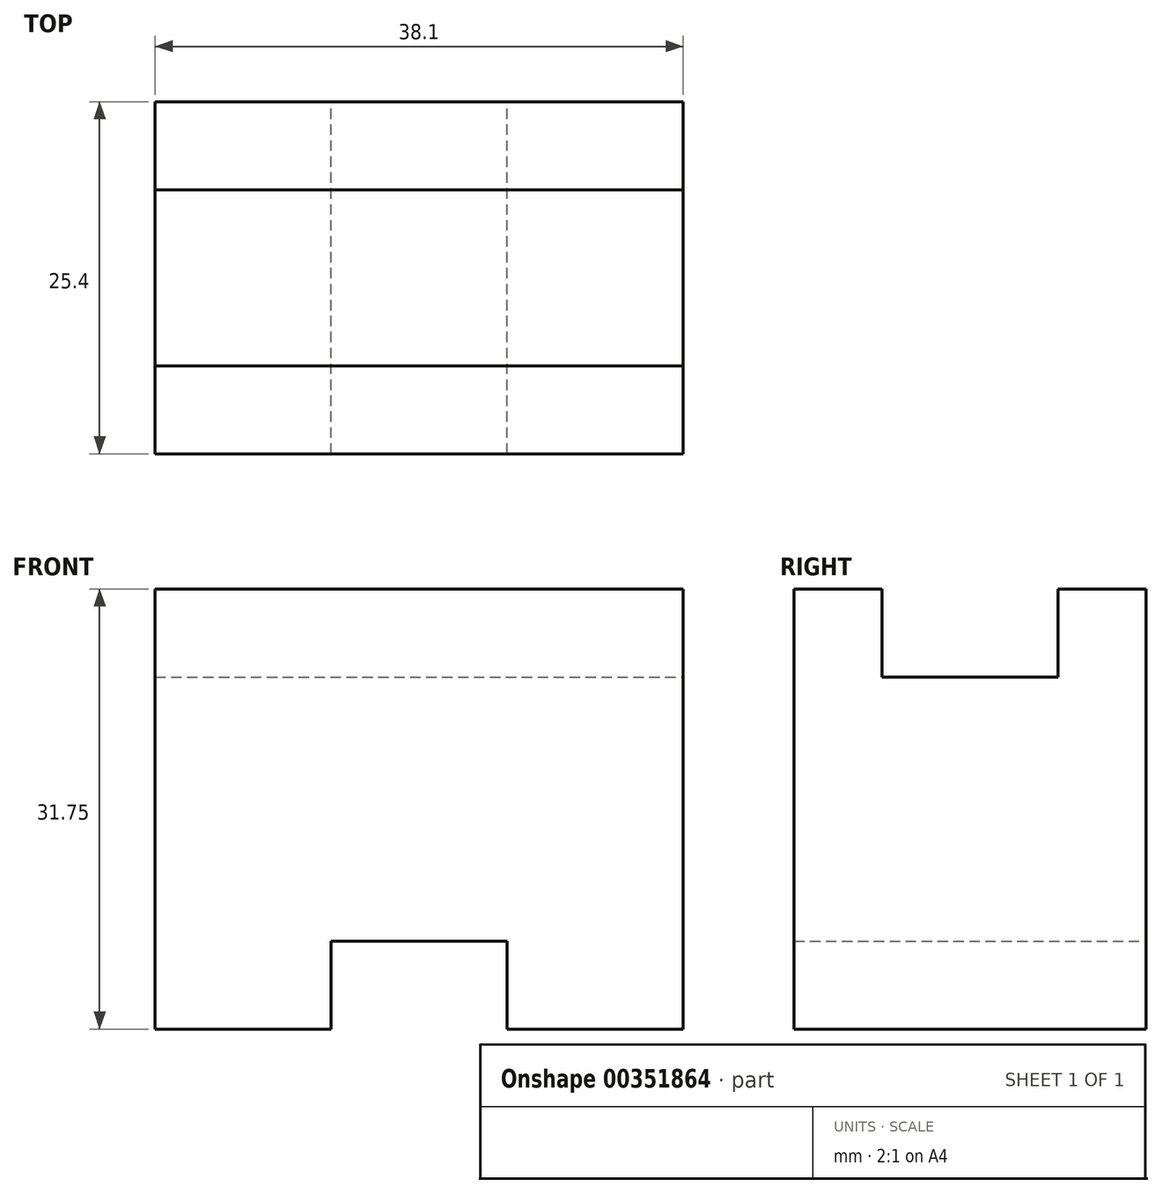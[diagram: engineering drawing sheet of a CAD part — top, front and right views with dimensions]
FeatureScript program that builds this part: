
annotation { "Feature Type Name" : "Feature", "Feature Type Description" : "" }
export const myFeature = defineFeature(function(context is Context, id is Id, definition is map)
    precondition{}
    {
        {
            var Q0;
            Q0=qCreatedBy(makeId("Front.planeOp"),FACE);
            var sketch = newSketch(context, id + "F0", { "sketchPlane" : qUnion([Q0])});
            skLineSegment(sketch, "E0", {"start": v(-46.75, 0) * mm, "end": v(-34.05, 0) * mm});
            skLineSegment(sketch, "E1", {"start": v(-34.05, 0) * mm, "end": v(-34.05, 6.35) * mm});
            skLineSegment(sketch, "E2", {"start": v(-34.05, 6.35) * mm, "end": v(-21.35, 6.35) * mm});
            skLineSegment(sketch, "E3", {"start": v(-21.35, 6.35) * mm, "end": v(-21.35, 0) * mm});
            skLineSegment(sketch, "E4", {"start": v(-21.35, 0) * mm, "end": v(-8.65, 0) * mm});
            skLineSegment(sketch, "E5", {"start": v(-8.65, 0) * mm, "end": v(-8.65, 31.75) * mm});
            skLineSegment(sketch, "E6", {"start": v(-46.75, 0) * mm, "end": v(-46.75, 31.75) * mm});
            skLineSegment(sketch, "E7", {"start": v(-46.75, 31.75) * mm, "end": v(-8.65, 31.75) * mm});
            skSolve(sketch);
        }
        {
            var Q0;
            Q0=makeQuery(id+"F0.imprint","IMPRINT",FACE,{"disambiguationData":[TD([[makeQuery(id+"F0.imprint","IMPRINT",EDGE,{"derivedFrom":sQuery(id+"F0.wireOp",EDGE,"E0")}),1.0]])]});
            extrude(context, id + "F1", {"entities" : qUnion([Q0]), "depth" : 25.4 * mm});
        }
        {
            var Q0;
            Q0=makeQuery(id+"F1.opExtrude","SWEPT_FACE",FACE,{"disambiguationData":[OSD([sQuery(id+"F0.wireOp",EDGE,"E5")])]});
            var sketch = newSketch(context, id + "F2", { "sketchPlane" : qUnion([Q0])});
            skLineSegment(sketch, "E8", {"start": v(-19.05, 31.75) * mm, "end": v(-19.05, 25.4) * mm});
            skLineSegment(sketch, "E9", {"start": v(-19.05, 25.4) * mm, "end": v(-6.35, 25.4) * mm});
            skLineSegment(sketch, "E10", {"start": v(-6.35, 25.4) * mm, "end": v(-6.35, 31.75) * mm});
            skLineSegment(sketch, "E11", {"start": v(-19.05, 31.75) * mm, "end": v(-6.35, 31.75) * mm});
            skSolve(sketch);
        }
        {
            var Q0;
            Q0 = qSketchRegion(id + "F2", true);
            extrude(context, id + "F3", {"entities" : qUnion([Q0]), "operationType" : NewBodyOperationType.REMOVE, "oppositeDirection" : true, "depth" : 38.1 * mm});
        }
    });
